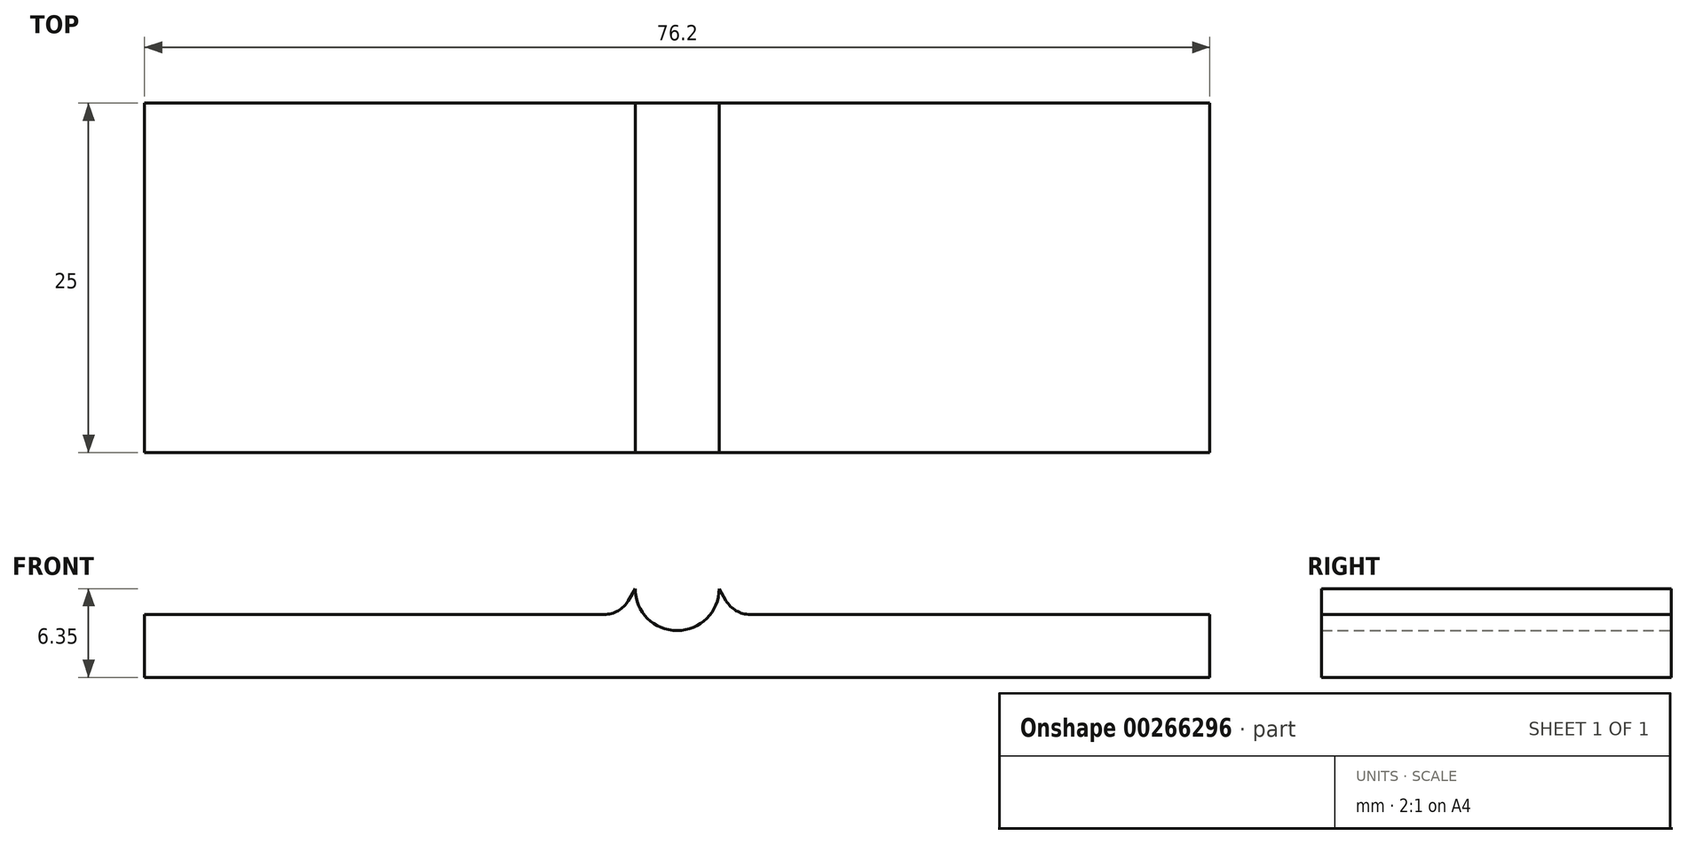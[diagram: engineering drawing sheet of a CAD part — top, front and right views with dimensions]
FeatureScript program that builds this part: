
annotation { "Feature Type Name" : "Feature", "Feature Type Description" : "" }
export const myFeature = defineFeature(function(context is Context, id is Id, definition is map)
    precondition{}
    {
        {
            var Q0;
            Q0=qCreatedBy(makeId("Front.planeOp"),FACE);
            var sketch = newSketch(context, id + "F0", { "sketchPlane" : qUnion([Q0])});
            skLineSegment(sketch, "E0.bottom", {"start": v(0, 0) * mm, "end": v(76.2, 0) * mm});
            skLineSegment(sketch, "E0.left", {"start": v(0, 0) * mm, "end": v(0, 4.5) * mm});
            skLineSegment(sketch, "E0.right", {"start": v(76.2, 0) * mm, "end": v(76.2, 4.5) * mm});
            skArc(sketch, "E1", {"start": v(35.1, 6.35) * mm, "mid": v(38.1, 3.35) * mm, "end": v(41.1, 6.35) * mm});
            skLineSegment(sketch, "E2", {"start": v(0, 4.5) * mm, "end": v(32.88, 4.5) * mm});
            skLineSegment(sketch, "E3", {"start": v(43.32, 4.5) * mm, "end": v(76.2, 4.5) * mm});
            skLineSegment(sketch, "E4", {"start": v(35.1, 6.35) * mm, "end": v(34.6, 5.5) * mm});
            skLineSegment(sketch, "E5", {"start": v(41.1, 6.35) * mm, "end": v(41.6, 5.5) * mm});
            skPoint(sketch, "E6.orphan", {"position": v(35.74, 4.5) * mm});
            skPoint(sketch, "E7.orphan", {"position": v(40.46, 4.5) * mm});
            skPoint(sketch, "E8.orphan", {"position": v(0, 6.35) * mm});
            skPoint(sketch, "E9.orphan", {"position": v(76.2, 6.35) * mm});
            skPoint(sketch, "E10.visualSharp", {"position": v(34.03, 4.5) * mm});
            skArc(sketch, "E10.filletArc", {"start": v(32.88, 4.5) * mm, "mid": v(33.88, 4.77) * mm, "end": v(34.6, 5.5) * mm});
            skPoint(sketch, "E11.visualSharp", {"position": v(42.17, 4.5) * mm});
            skArc(sketch, "E11.filletArc", {"start": v(41.6, 5.5) * mm, "mid": v(42.32, 4.77) * mm, "end": v(43.32, 4.5) * mm});
            skSolve(sketch);
        }
        {
            var Q0;
            Q0=makeQuery(id+"F0.imprint","IMPRINT",FACE,{"disambiguationData":[TD([[makeQuery(id+"F0.imprint","IMPRINT",EDGE,{"derivedFrom":sQuery(id+"F0.wireOp",EDGE,"E0.bottom")}),1.0]])]});
            extrude(context, id + "F1", {"entities" : qUnion([Q0]), "endBound" : BoundingType.SYMMETRIC, "depth" : 25 * mm});
        }
    });
